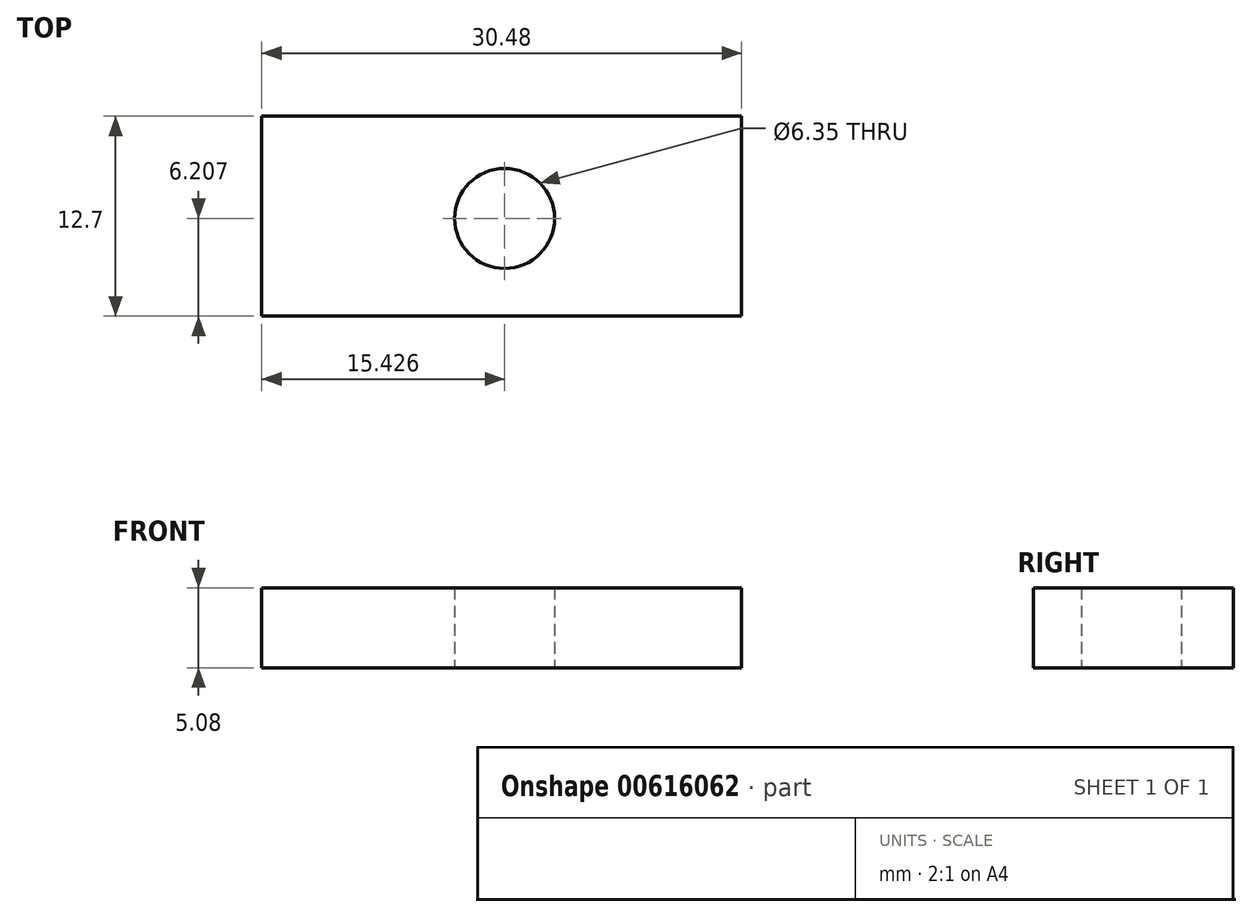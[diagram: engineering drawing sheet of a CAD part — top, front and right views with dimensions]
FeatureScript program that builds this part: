
annotation { "Feature Type Name" : "Feature", "Feature Type Description" : "" }
export const myFeature = defineFeature(function(context is Context, id is Id, definition is map)
    precondition{}
    {
        {
            var Q0;
            Q0=qCreatedBy(makeId("Top.planeOp"),FACE);
            var sketch = newSketch(context, id + "F0", { "sketchPlane" : qUnion([Q0])});
            skLineSegment(sketch, "E0.bottom", {"start": v(18.74, -10.96) * mm, "end": v(49.22, -10.96) * mm});
            skLineSegment(sketch, "E0.top", {"start": v(18.74, -23.66) * mm, "end": v(49.22, -23.66) * mm});
            skLineSegment(sketch, "E0.left", {"start": v(18.74, -10.96) * mm, "end": v(18.74, -23.66) * mm});
            skLineSegment(sketch, "E0.right", {"start": v(49.22, -10.96) * mm, "end": v(49.22, -23.66) * mm});
            skCircle(sketch, "E1", {"center": v(34.17, -17.45) * mm, "radius": 3.18 * mm});
            skSolve(sketch);
        }
        {
            var Q0;
            Q0 = qSketchRegion(id + "F0", true);
            extrude(context, id + "F1", {"entities" : qUnion([Q0]), "depth" : 5.08 * mm, "offsetDistance" : 25.4 * mm});
        }
    });
